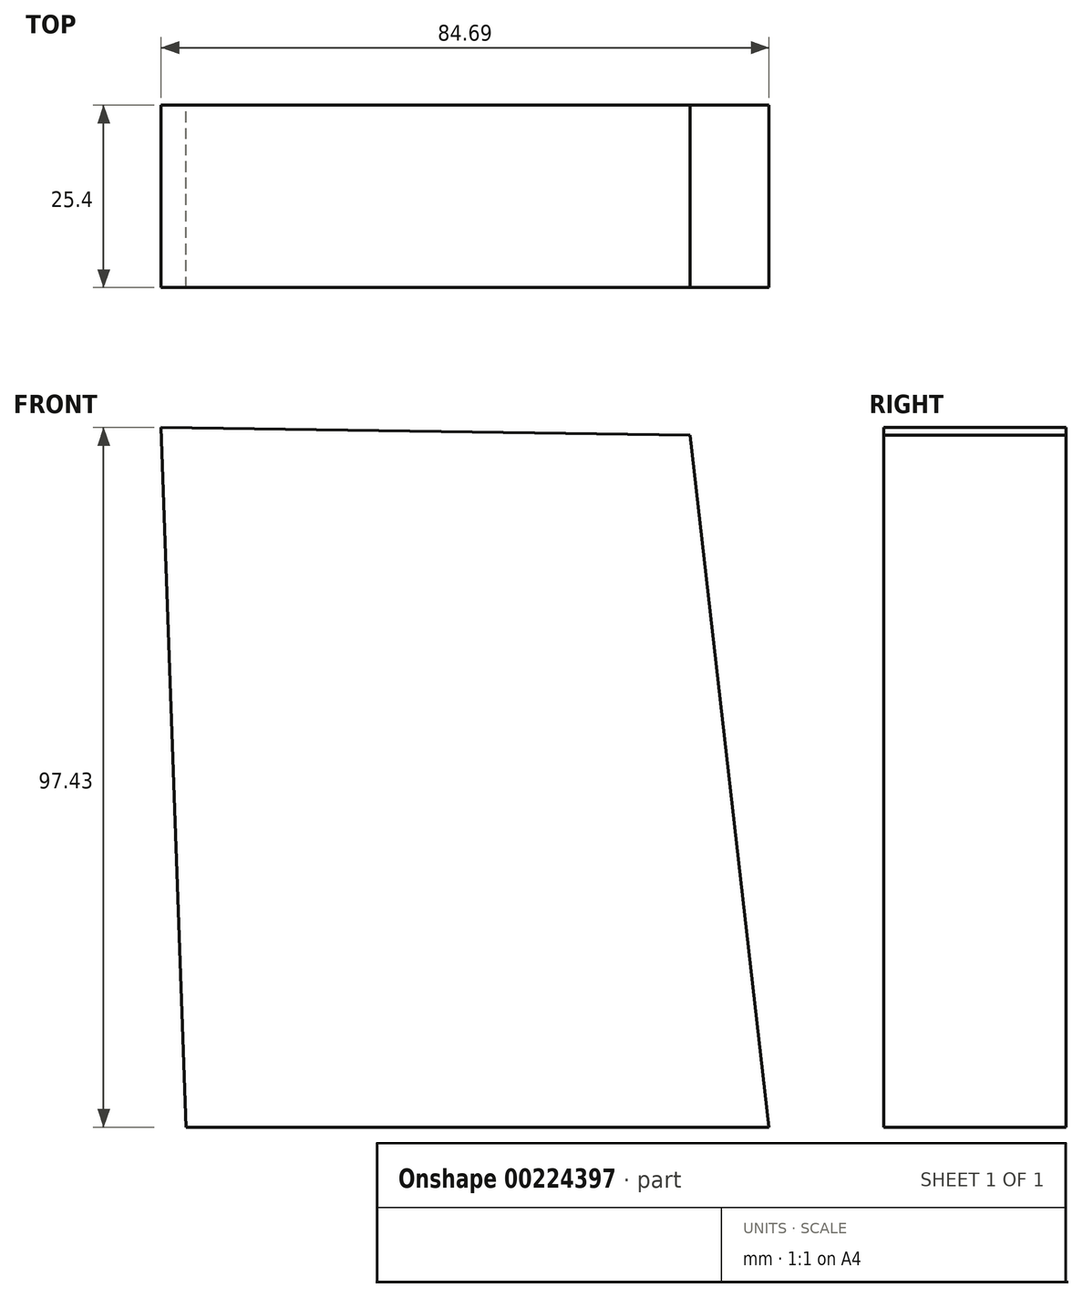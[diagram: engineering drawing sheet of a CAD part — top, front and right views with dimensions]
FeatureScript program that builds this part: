
annotation { "Feature Type Name" : "Feature", "Feature Type Description" : "" }
export const myFeature = defineFeature(function(context is Context, id is Id, definition is map)
    precondition{}
    {
        {
            var Q0;
            Q0=qCreatedBy(makeId("Front.planeOp"),FACE);
            var sketch = newSketch(context, id + "F0", { "sketchPlane" : qUnion([Q0])});
            skLineSegment(sketch, "E0", {"start": v(-56.29, 58.87) * mm, "end": v(-52.85, -38.56) * mm});
            skLineSegment(sketch, "E1", {"start": v(28.4, -38.56) * mm, "end": v(17.39, 57.84) * mm});
            skLineSegment(sketch, "E2", {"start": v(17.39, 57.84) * mm, "end": v(-56.29, 58.87) * mm});
            skLineSegment(sketch, "E3", {"start": v(-52.85, -38.56) * mm, "end": v(28.4, -38.56) * mm});
            skSolve(sketch);
        }
        {
            var Q0;
            Q0 = qSketchRegion(id + "F0", true);
            extrude(context, id + "F1", {"entities" : qUnion([Q0]), "depth" : 25.4 * mm});
        }
    });
